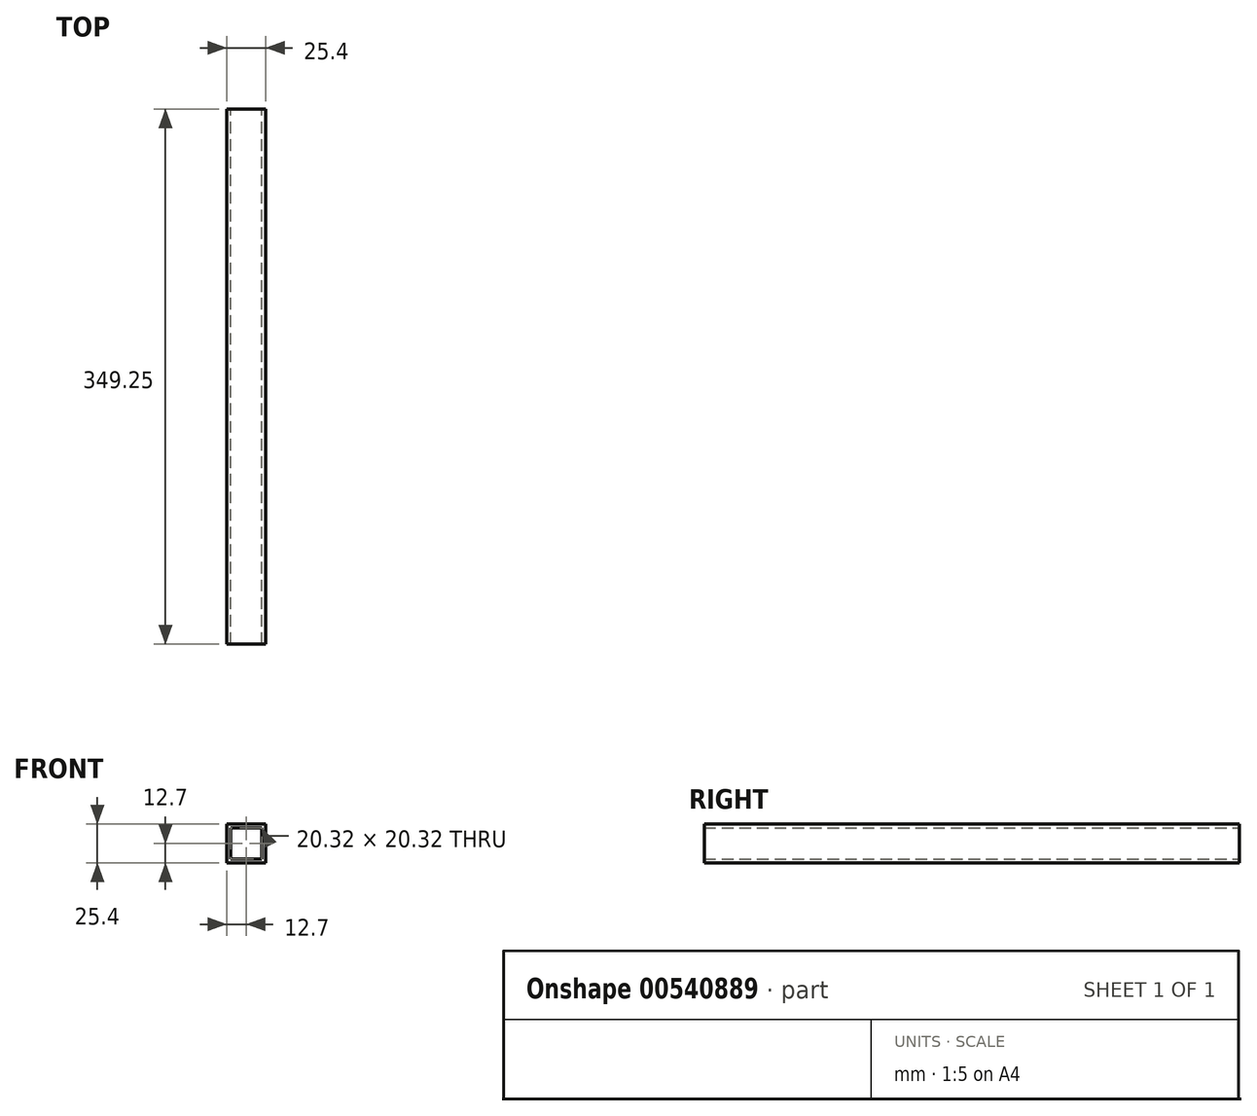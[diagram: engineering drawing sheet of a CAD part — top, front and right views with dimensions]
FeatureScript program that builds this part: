
annotation { "Feature Type Name" : "Feature", "Feature Type Description" : "" }
export const myFeature = defineFeature(function(context is Context, id is Id, definition is map)
    precondition{}
    {
        {
            var Q0;
            Q0=qCreatedBy(makeId("Front.planeOp"),FACE);
            var sketch = newSketch(context, id + "F0", { "sketchPlane" : qUnion([Q0])});
            skLineSegment(sketch, "E0.bottom", {"start": v(12.7, -12.7) * mm, "end": v(-12.7, -12.7) * mm});
            skLineSegment(sketch, "E0.top", {"start": v(12.7, 12.7) * mm, "end": v(-12.7, 12.7) * mm});
            skLineSegment(sketch, "E0.left", {"start": v(12.7, -12.7) * mm, "end": v(12.7, 12.7) * mm});
            skLineSegment(sketch, "E0.right", {"start": v(-12.7, -12.7) * mm, "end": v(-12.7, 12.7) * mm});
            skPoint(sketch, "E0.middle", {"position": v(0, 0) * mm});
            skLineSegment(sketch, "E1.bottom", {"start": v(10.16, -10.16) * mm, "end": v(-10.16, -10.16) * mm});
            skLineSegment(sketch, "E1.top", {"start": v(10.16, 10.16) * mm, "end": v(-10.16, 10.16) * mm});
            skLineSegment(sketch, "E1.left", {"start": v(10.16, -10.16) * mm, "end": v(10.16, 10.16) * mm});
            skLineSegment(sketch, "E1.right", {"start": v(-10.16, -10.16) * mm, "end": v(-10.16, 10.16) * mm});
            skSolve(sketch);
        }
        {
            var Q0;
            Q0 = qSketchRegion(id + "F0", true);
            extrude(context, id + "F1", {"entities" : qUnion([Q0]), "depth" : 349.25 * mm, "offsetDistance" : 25.4 * mm});
        }
    });
